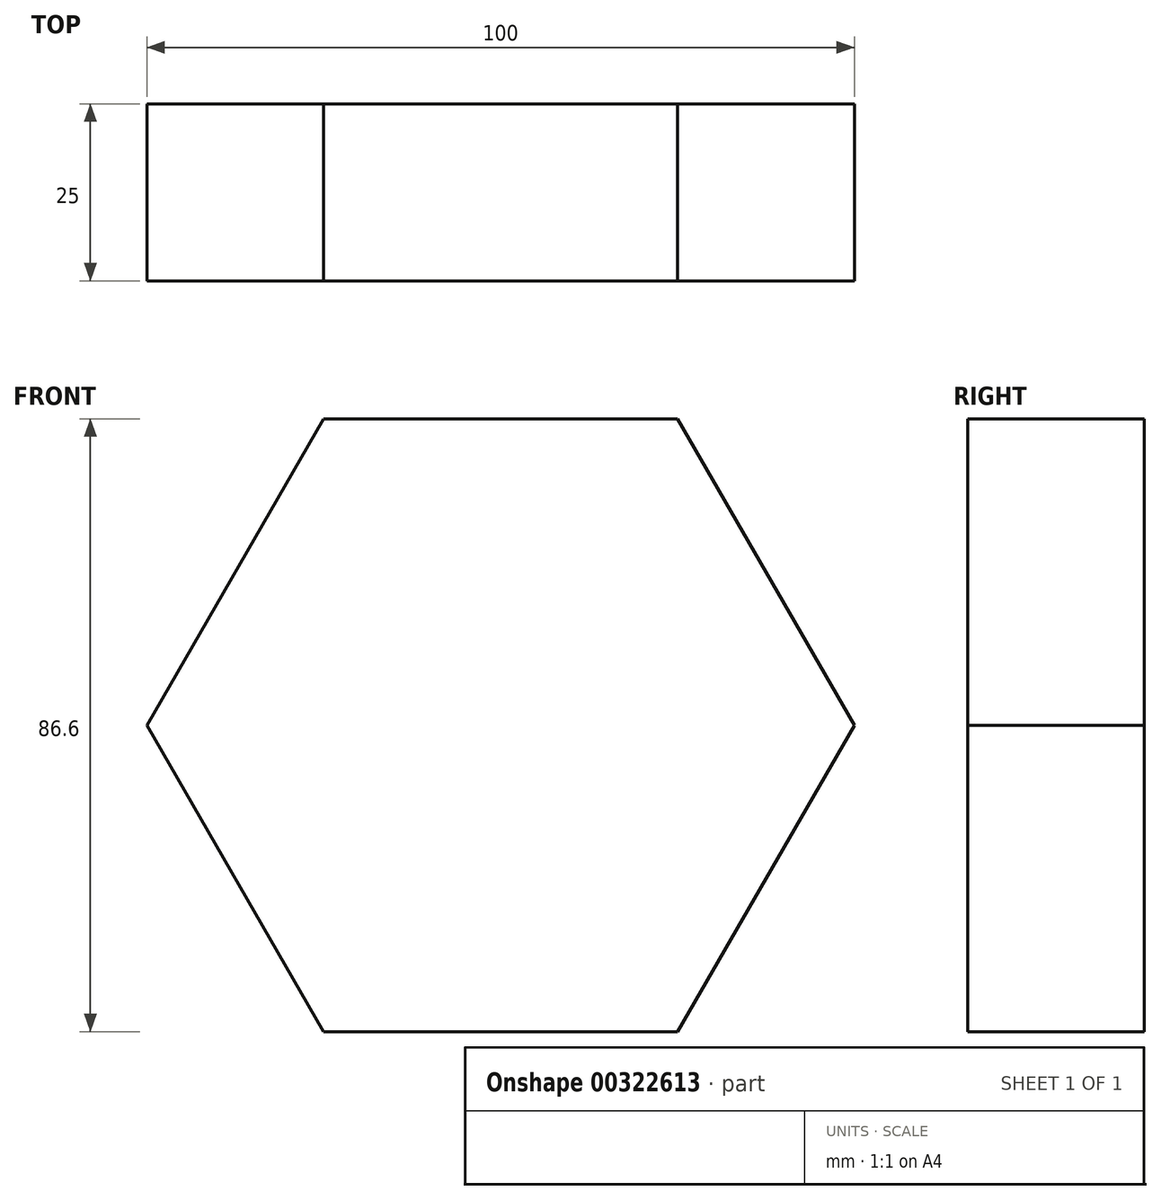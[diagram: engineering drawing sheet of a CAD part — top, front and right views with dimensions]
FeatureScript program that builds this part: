
annotation { "Feature Type Name" : "Feature", "Feature Type Description" : "" }
export const myFeature = defineFeature(function(context is Context, id is Id, definition is map)
    precondition{}
    {
        {
            var Q0;
            Q0=qCreatedBy(makeId("Front.planeOp"),FACE);
            var sketch = newSketch(context, id + "F0", { "sketchPlane" : qUnion([Q0])});
            skCircle(sketch, "E0.cCircle", {"center": v(0, 0) * mm, "radius": 43.3 * mm, "construction": true});
            skLineSegment(sketch, "E0.0", {"start": v(-25, 43.3) * mm, "end": v(25, 43.3) * mm});
            skLineSegment(sketch, "E0.1", {"start": v(25, 43.3) * mm, "end": v(50, 0) * mm});
            skLineSegment(sketch, "E0.2", {"start": v(50, 0) * mm, "end": v(25, -43.3) * mm});
            skLineSegment(sketch, "E0.3", {"start": v(25, -43.3) * mm, "end": v(-25, -43.3) * mm});
            skLineSegment(sketch, "E0.4", {"start": v(-25, -43.3) * mm, "end": v(-50, 0) * mm});
            skLineSegment(sketch, "E0.5", {"start": v(-50, 0) * mm, "end": v(-25, 43.3) * mm});
            skPoint(sketch, "E0.0.midPoint", {"position": v(0, 43.3) * mm});
            skSolve(sketch);
        }
        {
            var Q0;
            Q0=makeQuery(id+"F0.imprint","IMPRINT",FACE,{"disambiguationData":[TD([[makeQuery(id+"F0.imprint","IMPRINT",EDGE,{"derivedFrom":sQuery(id+"F0.wireOp",EDGE,"E0.0")}),-1.0]])]});
            extrude(context, id + "F1", {"entities" : qUnion([Q0]), "depth" : 25 * mm});
        }
    });
